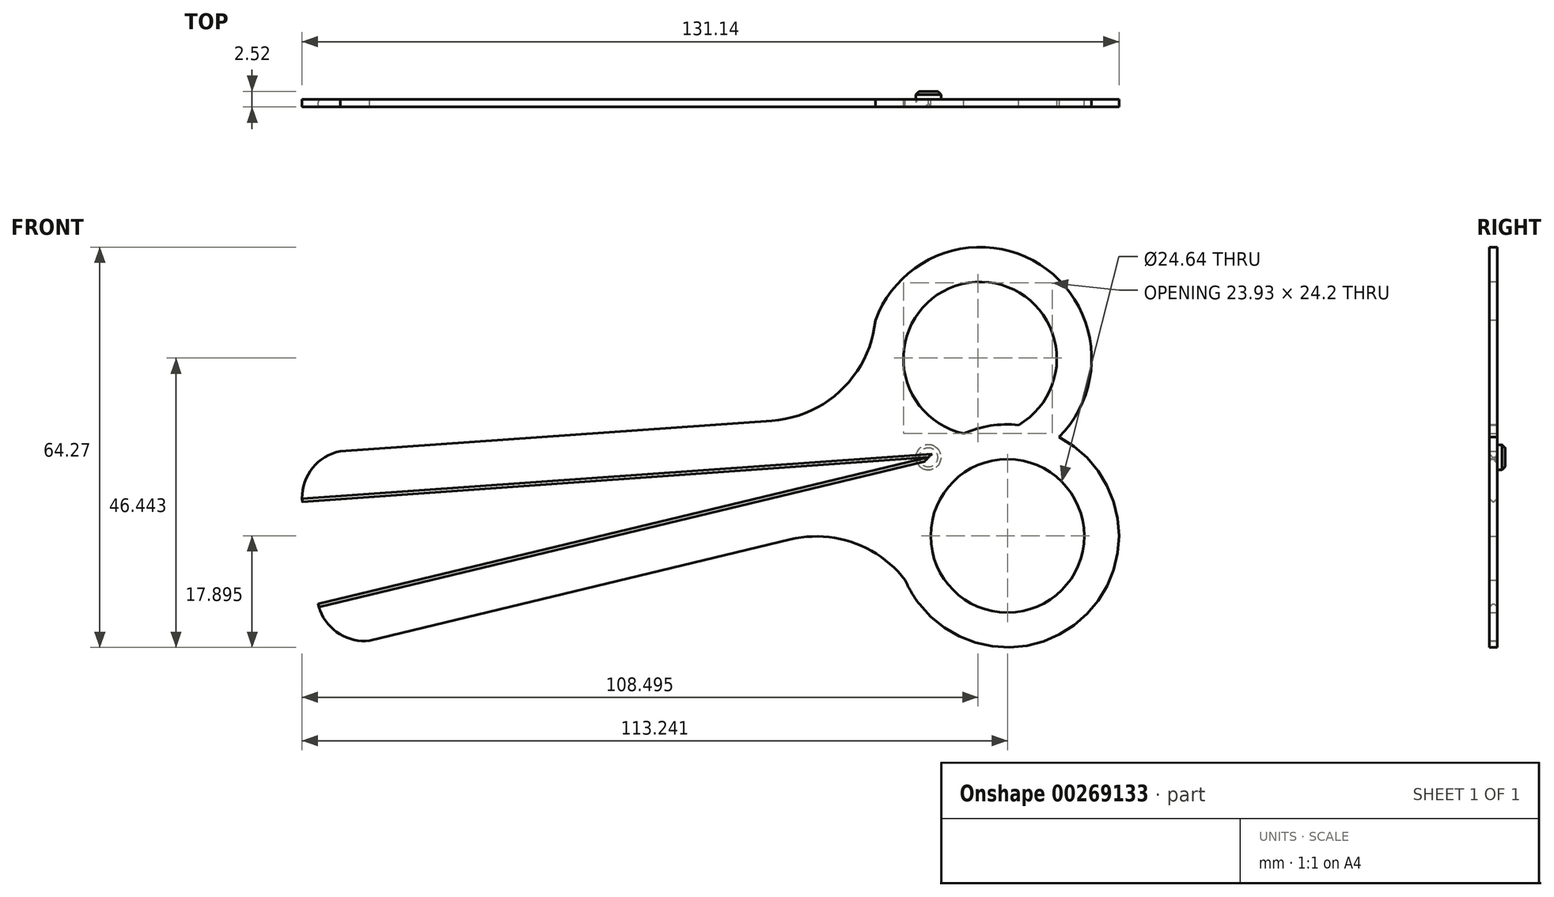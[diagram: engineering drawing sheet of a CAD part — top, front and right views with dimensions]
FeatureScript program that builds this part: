
annotation { "Feature Type Name" : "Feature", "Feature Type Description" : "" }
export const myFeature = defineFeature(function(context is Context, id is Id, definition is map)
    precondition{}
    {
        {
            var Q0;
            Q0=qCreatedBy(makeId("Front.planeOp"),FACE);
            var sketch = newSketch(context, id + "F0", { "sketchPlane" : qUnion([Q0])});
            skLineSegment(sketch, "E0", {"start": v(-113.66, 0) * mm, "end": v(-15.68, 23.55) * mm});
            skArc(sketch, "E1", {"start": v(-113.66, 0) * mm, "mid": v(-110.64, -4.52) * mm, "end": v(-105.37, -5.87) * mm});
            skLineSegment(sketch, "E2", {"start": v(-105.37, -5.87) * mm, "end": v(-37.88, 10.35) * mm});
            skArc(sketch, "E3", {"start": v(-17.15, 0) * mm, "mid": v(-25.63, 8.95) * mm, "end": v(-37.88, 10.35) * mm});
            skArc(sketch, "E4", {"start": v(-17.15, 0) * mm, "mid": v(14.89, 9.82) * mm, "end": v(-15.68, 23.55) * mm});
            skLineSegment(sketch, "E5", {"start": v(-15.68, 23.55) * mm, "end": v(-15.68, 23.55) * mm});
            skLineSegment(sketch, "E6.MirrorCS", {"start": v(-116.2, 16.43) * mm, "end": v(-15.68, 23.55) * mm});
            skArc(sketch, "E7.MirrorCS", {"start": v(-116.2, 16.43) * mm, "mid": v(-114.68, 21.65) * mm, "end": v(-110.07, 24.53) * mm});
            skLineSegment(sketch, "E8.MirrorCS", {"start": v(-110.07, 24.53) * mm, "end": v(-40.83, 29.43) * mm});
            skArc(sketch, "E9.MirrorCS", {"start": v(-24.19, 45.56) * mm, "mid": v(9.32, 45.87) * mm, "end": v(-15.68, 23.55) * mm});
            skArc(sketch, "E10.MirrorCS", {"start": v(-24.19, 45.56) * mm, "mid": v(-29.57, 34.46) * mm, "end": v(-40.83, 29.43) * mm});
            skSolve(sketch);
        }
        {
            var Q0;
            Q0 = qSketchRegion(id + "F0", true);
            extrude(context, id + "F1", {"entities" : qUnion([Q0]), "depth" : 1.25 * mm});
        }
        {
            var Q0;
            Q0=makeQuery(id+"F1.opExtrude","CAP_FACE",FACE,{"disambiguationData":[OSD([sQuery(id+"F0.wireOp",EDGE,"E0"),sQuery(id+"F0.wireOp",EDGE,"E1"),sQuery(id+"F0.wireOp",EDGE,"E2"),sQuery(id+"F0.wireOp",EDGE,"E3"),sQuery(id+"F0.wireOp",EDGE,"E4"),sQuery(id+"F0.wireOp",EDGE,"E6.MirrorCS"),sQuery(id+"F0.wireOp",EDGE,"E7.MirrorCS"),sQuery(id+"F0.wireOp",EDGE,"E8.MirrorCS"),sQuery(id+"F0.wireOp",EDGE,"E9.MirrorCS"),sQuery(id+"F0.wireOp",EDGE,"E10.MirrorCS")])],"isStart":false});
            var sketch = newSketch(context, id + "F2", { "sketchPlane" : qUnion([Q0])});
            skCircle(sketch, "E11", {"center": v(-7.38, 39.4) * mm, "radius": 12.32 * mm});
            skCircle(sketch, "E12", {"center": v(-2.98, 10.93) * mm, "radius": 12.32 * mm});
            skSolve(sketch);
        }
        {
            var Q0;
            Q0 = qSketchRegion(id + "F2", true);
            extrude(context, id + "F3", {"entities" : qUnion([Q0]), "operationType" : NewBodyOperationType.REMOVE, "oppositeDirection" : true, "depth" : 25.4 * mm});
        }
        {
            var Q0;
            Q0=makeQuery(id+"F1.opExtrude","CAP_FACE",FACE,{"disambiguationData":[OSD([sQuery(id+"F0.wireOp",EDGE,"E0"),sQuery(id+"F0.wireOp",EDGE,"E1"),sQuery(id+"F0.wireOp",EDGE,"E2"),sQuery(id+"F0.wireOp",EDGE,"E3"),sQuery(id+"F0.wireOp",EDGE,"E4"),sQuery(id+"F0.wireOp",EDGE,"E6.MirrorCS"),sQuery(id+"F0.wireOp",EDGE,"E7.MirrorCS"),sQuery(id+"F0.wireOp",EDGE,"E8.MirrorCS"),sQuery(id+"F0.wireOp",EDGE,"E9.MirrorCS"),sQuery(id+"F0.wireOp",EDGE,"E10.MirrorCS")])],"isStart":true});
            var sketch = newSketch(context, id + "F4", { "sketchPlane" : qUnion([Q0])});
            skCircle(sketch, "E13", {"center": v(15.68, 23.55) * mm, "radius": 2.02 * mm});
            skSolve(sketch);
        }
        {
            var Q0;
            Q0 = qSketchRegion(id + "F4", true);
            extrude(context, id + "F5", {"entities" : qUnion([Q0]), "operationType" : NewBodyOperationType.ADD, "depth" : 1.27 * mm});
        }
        {
            var Q0;
            {var subQ0=sQuery(id+"F0.wireOp",EDGE,"E0");Q0=makeQuery(id+"F5.boolean.opBoolean","SPLIT",EDGE,{"disambiguationData":[topologyDisambiguationEdgeConnected([makeQuery(id+"F1.opExtrude","CAP_FACE",FACE,{"disambiguationData":[OSD([subQ0,sQuery(id+"F0.wireOp",EDGE,"E1"),sQuery(id+"F0.wireOp",EDGE,"E2"),sQuery(id+"F0.wireOp",EDGE,"E3"),sQuery(id+"F0.wireOp",EDGE,"E4"),sQuery(id+"F0.wireOp",EDGE,"E6.MirrorCS"),sQuery(id+"F0.wireOp",EDGE,"E7.MirrorCS"),sQuery(id+"F0.wireOp",EDGE,"E8.MirrorCS"),sQuery(id+"F0.wireOp",EDGE,"E9.MirrorCS"),sQuery(id+"F0.wireOp",EDGE,"E10.MirrorCS")])],"isStart":true})])],"derivedFrom":makeQuery(id+"F1.opExtrude","CAP_EDGE",EDGE,{"disambiguationData":[OSD([subQ0])],"isStart":true})});}
            var Q1;
            Q1=makeQuery(id+"F1.opExtrude","CAP_EDGE",EDGE,{"disambiguationData":[OSD([sQuery(id+"F0.wireOp",EDGE,"E0")])],"isStart":false});
            var Q2;
            {var subQ0=sQuery(id+"F0.wireOp",EDGE,"E6.MirrorCS");Q2=makeQuery(id+"F5.boolean.opBoolean","SPLIT",EDGE,{"disambiguationData":[topologyDisambiguationEdgeConnected([makeQuery(id+"F1.opExtrude","CAP_FACE",FACE,{"disambiguationData":[OSD([sQuery(id+"F0.wireOp",EDGE,"E0"),sQuery(id+"F0.wireOp",EDGE,"E1"),sQuery(id+"F0.wireOp",EDGE,"E2"),sQuery(id+"F0.wireOp",EDGE,"E3"),sQuery(id+"F0.wireOp",EDGE,"E4"),subQ0,sQuery(id+"F0.wireOp",EDGE,"E7.MirrorCS"),sQuery(id+"F0.wireOp",EDGE,"E8.MirrorCS"),sQuery(id+"F0.wireOp",EDGE,"E9.MirrorCS"),sQuery(id+"F0.wireOp",EDGE,"E10.MirrorCS")])],"isStart":true})])],"derivedFrom":makeQuery(id+"F1.opExtrude","CAP_EDGE",EDGE,{"disambiguationData":[OSD([subQ0])],"isStart":true})});}
            var Q3;
            Q3=makeQuery(id+"F1.opExtrude","CAP_EDGE",EDGE,{"disambiguationData":[OSD([sQuery(id+"F0.wireOp",EDGE,"E6.MirrorCS")])],"isStart":false});
            chamfer(context, id + "F6", {"entities" : qUnion([Q0, Q1, Q2, Q3]), "width" : 0.5 * mm, "tangentPropagation" : true});
        }
        {
            var Q0;
            {var subQ0=sQuery(id+"F0.wireOp",EDGE,"E6.MirrorCS");var subQ1=makeQuery(id+"F1.opExtrude","SWEPT_FACE",FACE,{"disambiguationData":[OSD([subQ0])]});Q0=makeQuery(id+"F6.opChamfer","BLEND_EDGE",EDGE,{"blendedFrom":[makeQuery(id+"F5.boolean.opBoolean","SPLIT",EDGE,{"disambiguationData":[topologyDisambiguationEdgeConnected([makeQuery(id+"F1.opExtrude","CAP_FACE",FACE,{"disambiguationData":[OSD([sQuery(id+"F0.wireOp",EDGE,"E0"),sQuery(id+"F0.wireOp",EDGE,"E1"),sQuery(id+"F0.wireOp",EDGE,"E2"),sQuery(id+"F0.wireOp",EDGE,"E3"),sQuery(id+"F0.wireOp",EDGE,"E4"),subQ0,sQuery(id+"F0.wireOp",EDGE,"E7.MirrorCS"),sQuery(id+"F0.wireOp",EDGE,"E8.MirrorCS"),sQuery(id+"F0.wireOp",EDGE,"E9.MirrorCS"),sQuery(id+"F0.wireOp",EDGE,"E10.MirrorCS")])],"isStart":true})])],"derivedFrom":makeQuery(id+"F1.opExtrude","CAP_EDGE",EDGE,{"disambiguationData":[OSD([subQ0])],"isStart":true})}),subQ1],"blendedInto":[subQ1]});}
            var Q1;
            {var subQ0=sQuery(id+"F0.wireOp",EDGE,"E6.MirrorCS");Q1=makeQuery(id+"F6.opChamfer","BLEND_EDGE",EDGE,{"blendedFrom":[makeQuery(id+"F1.opExtrude","CAP_EDGE",EDGE,{"disambiguationData":[OSD([subQ0])],"isStart":false}),makeQuery(id+"F1.opExtrude","SWEPT_FACE",FACE,{"disambiguationData":[OSD([subQ0])]})],"blendedInto":[makeQuery(id+"F1.opExtrude","SWEPT_FACE",FACE,{"disambiguationData":[OSD([subQ0])]})]});}
            var Q2;
            {var subQ0=sQuery(id+"F0.wireOp",EDGE,"E0");Q2=makeQuery(id+"F6.opChamfer","BLEND_EDGE",EDGE,{"blendedFrom":[makeQuery(id+"F1.opExtrude","CAP_EDGE",EDGE,{"disambiguationData":[OSD([subQ0])],"isStart":false}),makeQuery(id+"F1.opExtrude","SWEPT_FACE",FACE,{"disambiguationData":[OSD([subQ0])]})],"blendedInto":[makeQuery(id+"F1.opExtrude","SWEPT_FACE",FACE,{"disambiguationData":[OSD([subQ0])]})]});}
            var Q3;
            {var subQ0=sQuery(id+"F0.wireOp",EDGE,"E0");var subQ1=makeQuery(id+"F1.opExtrude","SWEPT_FACE",FACE,{"disambiguationData":[OSD([subQ0])]});Q3=makeQuery(id+"F6.opChamfer","BLEND_EDGE",EDGE,{"blendedFrom":[makeQuery(id+"F5.boolean.opBoolean","SPLIT",EDGE,{"disambiguationData":[topologyDisambiguationEdgeConnected([makeQuery(id+"F1.opExtrude","CAP_FACE",FACE,{"disambiguationData":[OSD([subQ0,sQuery(id+"F0.wireOp",EDGE,"E1"),sQuery(id+"F0.wireOp",EDGE,"E2"),sQuery(id+"F0.wireOp",EDGE,"E3"),sQuery(id+"F0.wireOp",EDGE,"E4"),sQuery(id+"F0.wireOp",EDGE,"E6.MirrorCS"),sQuery(id+"F0.wireOp",EDGE,"E7.MirrorCS"),sQuery(id+"F0.wireOp",EDGE,"E8.MirrorCS"),sQuery(id+"F0.wireOp",EDGE,"E9.MirrorCS"),sQuery(id+"F0.wireOp",EDGE,"E10.MirrorCS")])],"isStart":true})])],"derivedFrom":makeQuery(id+"F1.opExtrude","CAP_EDGE",EDGE,{"disambiguationData":[OSD([subQ0])],"isStart":true})}),subQ1],"blendedInto":[subQ1]});}
            fillet(context, id + "F7", {"entities" : qUnion([Q0, Q1, Q2, Q3]), "radius" : 0.03 * mm, "tangentPropagation" : true, "allowEdgeOverflow" : false});
        }
        {
            var Q0;
            Q0=makeQuery(id+"F1.opExtrude","SWEPT_BODY",BODY,{"disambiguationData":[OSD([sQuery(id+"F0.wireOp",EDGE,"E0"),sQuery(id+"F0.wireOp",EDGE,"E1"),sQuery(id+"F0.wireOp",EDGE,"E2"),sQuery(id+"F0.wireOp",EDGE,"E3"),sQuery(id+"F0.wireOp",EDGE,"E4"),sQuery(id+"F0.wireOp",EDGE,"E6.MirrorCS"),sQuery(id+"F0.wireOp",EDGE,"E7.MirrorCS"),sQuery(id+"F0.wireOp",EDGE,"E8.MirrorCS"),sQuery(id+"F0.wireOp",EDGE,"E9.MirrorCS"),sQuery(id+"F0.wireOp",EDGE,"E10.MirrorCS")])]});
            var Q1;
            Q1=makeQuery(id+"F3.boolean.opBoolean","INTERSECT",EDGE,{"derivedFrom":[makeQuery(id+"F1.opExtrude","CAP_FACE",FACE,{"disambiguationData":[OSD([sQuery(id+"F0.wireOp",EDGE,"E0"),sQuery(id+"F0.wireOp",EDGE,"E1"),sQuery(id+"F0.wireOp",EDGE,"E2"),sQuery(id+"F0.wireOp",EDGE,"E3"),sQuery(id+"F0.wireOp",EDGE,"E4"),sQuery(id+"F0.wireOp",EDGE,"E6.MirrorCS"),sQuery(id+"F0.wireOp",EDGE,"E7.MirrorCS"),sQuery(id+"F0.wireOp",EDGE,"E8.MirrorCS"),sQuery(id+"F0.wireOp",EDGE,"E9.MirrorCS"),sQuery(id+"F0.wireOp",EDGE,"E10.MirrorCS")])],"isStart":true}),makeQuery(id+"F3.opExtrude","SWEPT_FACE",FACE,{"disambiguationData":[OSD([sQuery(id+"F2.wireOp",EDGE,"E11")])]})]});
            circularPattern(context, id + "F8", {"operationType" : NewBodyOperationType.ADD, "entities" : qUnion([Q0]), "axis" : qUnion([Q1]), "angle" : 360 * degree, "instanceCount" : 2, "oppositeDirection" : true, "equalSpace" : true});
        }
        {
            var Q0;
            Q0=makeQuery(id+"F8.boolean.opBoolean","SPLIT",EDGE,{"derivedFrom":makeQuery(id+"F5.opExtrude","CAP_EDGE",EDGE,{"disambiguationData":[OSD([sQuery(id+"F4.wireOp",EDGE,"E13")])],"isStart":false})});
            var Q1;
            {var subQ0=makeQuery(id+"F5.opExtrude","CAP_EDGE",EDGE,{"disambiguationData":[OSD([sQuery(id+"F4.wireOp",EDGE,"E13")])],"isStart":false});Q1=makeQuery(id+"F8.boolean.opBoolean","MERGE",EDGE,{"derivedFrom":[subQ0,makeQuery(id+"F8.opPattern","COPY",EDGE,{"derivedFrom":subQ0,"instanceName":"1"})]});}
            chamfer(context, id + "F9", {"entities" : qUnion([Q0, Q1]), "width" : 0.5 * mm, "tangentPropagation" : true});
        }
        {
            var Q0;
            {var subQ0=makeQuery(id+"F1.opExtrude","CAP_FACE",FACE,{"disambiguationData":[OSD([sQuery(id+"F0.wireOp",EDGE,"E0"),sQuery(id+"F0.wireOp",EDGE,"E1"),sQuery(id+"F0.wireOp",EDGE,"E2"),sQuery(id+"F0.wireOp",EDGE,"E3"),sQuery(id+"F0.wireOp",EDGE,"E4"),sQuery(id+"F0.wireOp",EDGE,"E6.MirrorCS"),sQuery(id+"F0.wireOp",EDGE,"E7.MirrorCS"),sQuery(id+"F0.wireOp",EDGE,"E8.MirrorCS"),sQuery(id+"F0.wireOp",EDGE,"E9.MirrorCS"),sQuery(id+"F0.wireOp",EDGE,"E10.MirrorCS")])],"isStart":true});Q0=makeQuery(id+"F8.boolean.opBoolean","MERGE",FACE,{"derivedFrom":[subQ0,makeQuery(id+"F8.opPattern","COPY",FACE,{"derivedFrom":subQ0,"instanceName":"1"})]});}
            var sketch = newSketch(context, id + "F10", { "sketchPlane" : qUnion([Q0])});
            skCircle(sketch, "E14", {"center": v(2.98, 10.93) * mm, "radius": 17.9 * mm});
            skSolve(sketch);
        }
        {
            var Q0;
            Q0 = qSketchRegion(id + "F10", true);
            extrude(context, id + "F11", {"entities" : qUnion([Q0]), "operationType" : NewBodyOperationType.ADD, "oppositeDirection" : true, "depth" : 1.25 * mm});
        }
        {
            var Q0;
            {var subQ0=makeQuery(id+"F1.opExtrude","CAP_FACE",FACE,{"disambiguationData":[OSD([sQuery(id+"F0.wireOp",EDGE,"E0"),sQuery(id+"F0.wireOp",EDGE,"E1"),sQuery(id+"F0.wireOp",EDGE,"E2"),sQuery(id+"F0.wireOp",EDGE,"E3"),sQuery(id+"F0.wireOp",EDGE,"E4"),sQuery(id+"F0.wireOp",EDGE,"E6.MirrorCS"),sQuery(id+"F0.wireOp",EDGE,"E7.MirrorCS"),sQuery(id+"F0.wireOp",EDGE,"E8.MirrorCS"),sQuery(id+"F0.wireOp",EDGE,"E9.MirrorCS"),sQuery(id+"F0.wireOp",EDGE,"E10.MirrorCS")])],"isStart":true});Q0=makeQuery(id+"F11.boolean.opBoolean","MERGE",FACE,{"derivedFrom":[makeQuery(id+"F8.boolean.opBoolean","MERGE",FACE,{"derivedFrom":[subQ0,makeQuery(id+"F8.opPattern","COPY",FACE,{"derivedFrom":subQ0,"instanceName":"1"})]}),makeQuery(id+"F11.opExtrude","CAP_FACE",FACE,{"disambiguationData":[OSD([sQuery(id+"F10.wireOp",EDGE,"E14")])],"isStart":true})]});}
            var sketch = newSketch(context, id + "F12", { "sketchPlane" : qUnion([Q0])});
            skCircle(sketch, "E15", {"center": v(2.98, 10.93) * mm, "radius": 12.32 * mm});
            skSolve(sketch);
        }
        {
            var Q0;
            Q0 = qSketchRegion(id + "F12", true);
            extrude(context, id + "F13", {"entities" : qUnion([Q0]), "operationType" : NewBodyOperationType.REMOVE, "oppositeDirection" : true, "depth" : 25.4 * mm});
        }
    });
